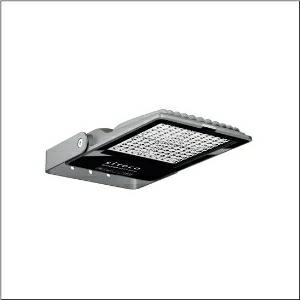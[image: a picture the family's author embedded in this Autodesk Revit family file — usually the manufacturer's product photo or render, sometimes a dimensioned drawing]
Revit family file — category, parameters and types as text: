
# Revit family: sicompact_r__31_mini___pl32_5xa7571b1k23_124a
name_source: partatom
category: Lighting Fixtures
units: mm (PartAtom-declared; Revit-internal decimal feet)

## family parameters
Cut with Voids When Loaded = No
Host = Face
Light Source = No
Part Type = Normal
Room Calculation Point = No
Round Connector Dimension = Use Diameter
Shared = No

## types (1)
- SiCompact® 31 mini  PL32 (1 x LED, 8000 lm, 48 W, 3000K)
    Apparent Load = 48 VA
    CIE Flux Codes = 32 69 98 100 100
    Color Rendering = 70
    Color Temperature = 3000K
    Default Elevation = 1800 mm
    Description = SiCompact® 31 mini, floodlight, primary light control with lens, of plastic, of toughened safety glass, transparent, light distribution: PL32, light emission: direct distribution, primary light characteristic: asymmetric, installation type: surface-mounted, LED, High Power LED, rated luminous flux: 8.000lm, luminous efficacy: 167lm/W, light colour: 730, colour temperature: 3000K, control gear: ON/OFF, with cable, 3x 1.5mm², mains connection: 220..240V, AC, 50/60Hz, connection cable pre-assembled, cable length: 2m, rated input power: 48W, of diecast aluminium, specular, metallic grey (RAL 9006), length: 461mm, width: 261mm, height: 62mm, bracket, of sheet steel, coated, metallic grey (RAL 9006), ON/OFF, protection rating (complete): IP66, insulation class (complete): insulation class I (protective earthing), certification: CE, ENEC, impact resistance: IK08, permissible operating ambient temperature: -40..+45°C, packaging unit: 1 piece

Light Distribution: PL32
    Height = 62 mm  [stored 0.203412 ft]
    Lamp = 1 x LED
    Lamp Light Flux = 8000 lm
    Lamp Power = 48 W
    Lamp count = 1
    Length = 460 mm
    Luminous efficacy = 167 lm/W
    Manufacturer = Siteco
    ModVariant = No
    Model = 5XA7571B1K23
    Mounting Place = Wall
    Mounting Type = Surface mounted
    Number of Poles = 1
    OnlyDefault = Yes
    Power Factor = 1
    Product Name = SiCompact® 31 mini | PL32
    Product group = floodlight | wall mounted
    ProductGroupID = 2001
    Protection Class = Protection class I
    Protection Degree = IP 66
    RLX_Detail_Level = 1
    RLX_Emergency_Light_Flux = 0 lm
    RLX_Emergency_Type = 0
    RLX_Emergency_Type_DB = No
    RlxData = <blob elided: 126657 chars, md5=08804971>
    Socket = socket
    Standby Power = 0 W
    System Light Flux = 8000 lm
    System Power = 48 W
    Type Comments = Product without accessories
    Type Image = l_1006951.jpg
    URL = http://relux.com
    VarID = ---
    Voltage = 0 V
    Weight = 0.00 kg
    Width = 260 mm

note: [stored X ft] marks values corroborated as IEEE doubles in the binary element streams (Revit-internal decimal feet)

## geometry (parser evidence)
native form markers: Blend x4, Sweep x15
no freeform markers — native parametric forms only
